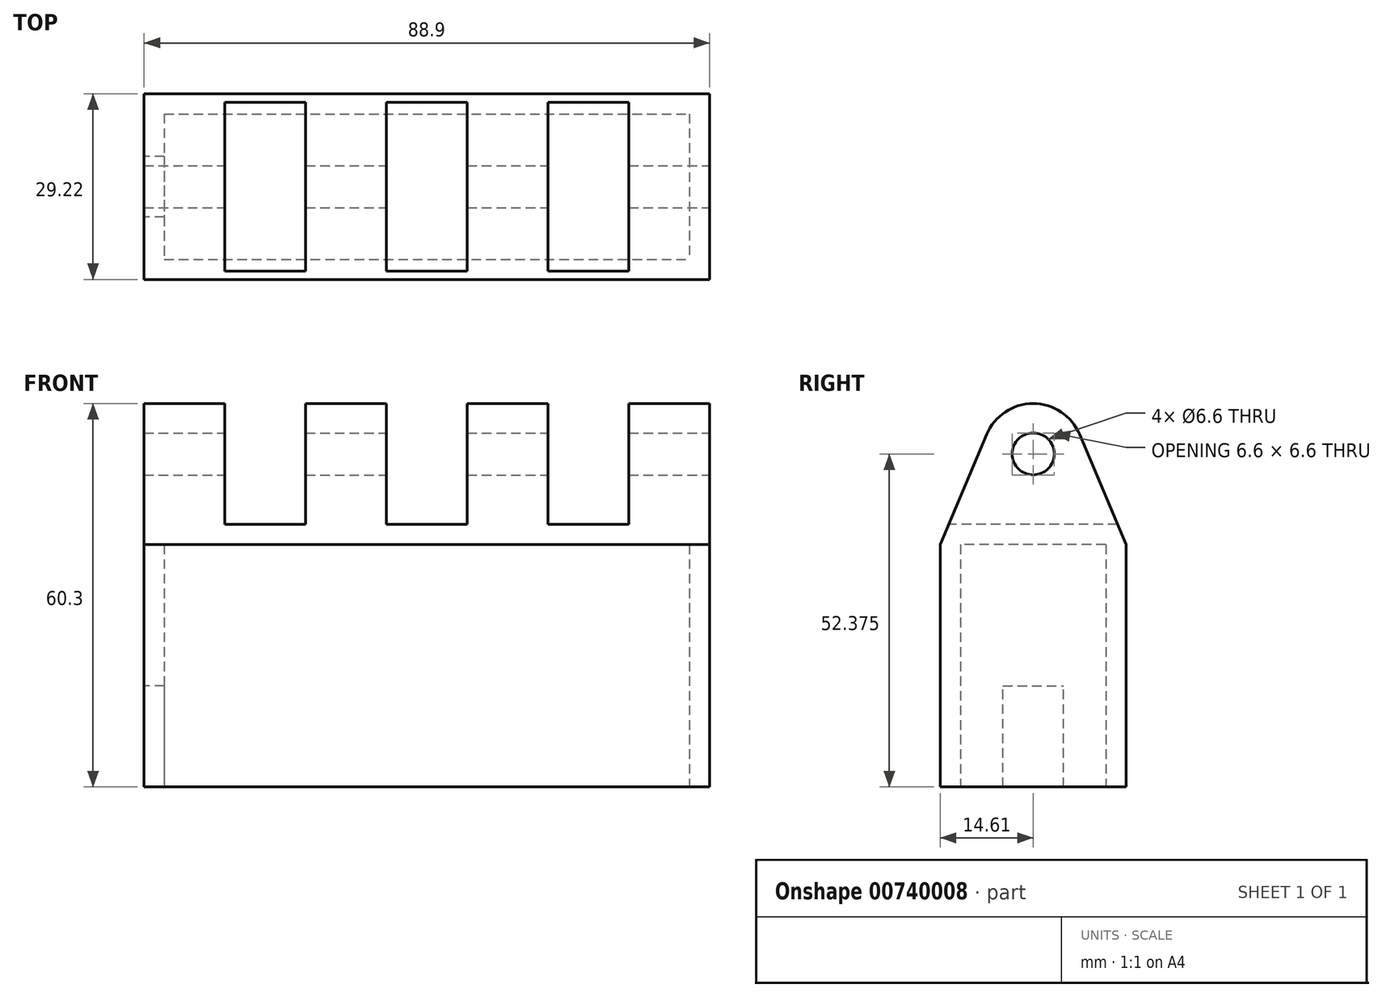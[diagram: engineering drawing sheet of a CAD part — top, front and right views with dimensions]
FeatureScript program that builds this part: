
annotation { "Feature Type Name" : "Feature", "Feature Type Description" : "" }
export const myFeature = defineFeature(function(context is Context, id is Id, definition is map)
    precondition{}
    {
        {
            var Q0;
            Q0=qCreatedBy(makeId("Top.planeOp"),FACE);
            var sketch = newSketch(context, id + "F0", { "sketchPlane" : qUnion([Q0])});
            skLineSegment(sketch, "E0.bottom", {"start": v(-41.28, 11.43) * mm, "end": v(41.28, 11.43) * mm});
            skLineSegment(sketch, "E0.top", {"start": v(-41.28, -11.43) * mm, "end": v(41.28, -11.43) * mm});
            skLineSegment(sketch, "E0.left", {"start": v(-41.28, 11.43) * mm, "end": v(-41.28, -11.43) * mm});
            skLineSegment(sketch, "E0.right", {"start": v(41.28, 11.43) * mm, "end": v(41.28, -11.43) * mm});
            skLineSegment(sketch, "E1.bottom", {"start": v(-44.45, 14.6) * mm, "end": v(44.45, 14.6) * mm});
            skLineSegment(sketch, "E1.top", {"start": v(-44.45, -14.6) * mm, "end": v(44.45, -14.6) * mm});
            skLineSegment(sketch, "E1.left", {"start": v(-44.45, 14.6) * mm, "end": v(-44.45, -14.6) * mm});
            skLineSegment(sketch, "E1.right", {"start": v(44.45, 14.6) * mm, "end": v(44.45, -14.6) * mm});
            skSolve(sketch);
        }
        {
            var Q0;
            Q0=makeQuery(id+"F0.imprint","IMPRINT",FACE,{"disambiguationData":[TD([[makeQuery(id+"F0.imprint","IMPRINT",EDGE,{"derivedFrom":sQuery(id+"F0.wireOp",EDGE,"E0.bottom")}),1.0]])]});
            extrude(context, id + "F1", {"entities" : qUnion([Q0]), "depth" : 38.1 * mm, "offsetDistance" : 25.4 * mm});
        }
        {
            var Q0;
            Q0=makeQuery(id+"F1.opExtrude","SWEPT_FACE",FACE,{"disambiguationData":[OSD([sQuery(id+"F0.wireOp",EDGE,"E1.left")])]});
            var sketch = newSketch(context, id + "F2", { "sketchPlane" : qUnion([Q0])});
            skLineSegment(sketch, "E2.bottom", {"start": v(4.76, 0) * mm, "end": v(-4.76, 0) * mm});
            skLineSegment(sketch, "E2.top", {"start": v(4.76, 15.88) * mm, "end": v(-4.76, 15.88) * mm});
            skLineSegment(sketch, "E2.left", {"start": v(4.76, 0) * mm, "end": v(4.76, 15.88) * mm});
            skLineSegment(sketch, "E2.right", {"start": v(-4.76, 0) * mm, "end": v(-4.76, 15.88) * mm});
            skSolve(sketch);
        }
        {
            var Q0;
            Q0=makeQuery(id+"F2.imprint","IMPRINT",FACE,{"disambiguationData":[TD([[makeQuery(id+"F2.imprint","IMPRINT",EDGE,{"derivedFrom":sQuery(id+"F2.wireOp",EDGE,"E2.bottom")}),1.0]])]});
            extrude(context, id + "F3", {"entities" : qUnion([Q0]), "operationType" : NewBodyOperationType.REMOVE, "oppositeDirection" : true, "depth" : 25.4 * mm, "offsetDistance" : 25.4 * mm});
        }
        {
            var Q0;
            Q0=makeQuery(id+"F1.opExtrude","SWEPT_FACE",FACE,{"disambiguationData":[OSD([sQuery(id+"F0.wireOp",EDGE,"E1.right")])]});
            var sketch = newSketch(context, id + "F4", { "sketchPlane" : qUnion([Q0])});
            skArc(sketch, "E3", {"start": v(7.3, 55.45) * mm, "mid": v(0, 60.3) * mm, "end": v(-7.3, 55.45) * mm});
            skLineSegment(sketch, "E4", {"start": v(-14.6, 38.1) * mm, "end": v(-7.3, 55.45) * mm});
            skLineSegment(sketch, "E5", {"start": v(14.6, 38.1) * mm, "end": v(7.3, 55.45) * mm});
            skLineSegment(sketch, "E6", {"start": v(-14.6, 38.1) * mm, "end": v(14.6, 38.1) * mm});
            skSolve(sketch);
        }
        {
            var Q0;
            Q0=makeQuery(id+"F4.imprint","IMPRINT",FACE,{"disambiguationData":[TD([[makeQuery(id+"F4.imprint","IMPRINT",EDGE,{"derivedFrom":sQuery(id+"F4.wireOp",EDGE,"E3")}),1.0]])]});
            var Q1;
            Q1=makeQuery(id+"F1.opExtrude","SWEPT_FACE",FACE,{"disambiguationData":[OSD([sQuery(id+"F0.wireOp",EDGE,"E1.left")])]});
            extrude(context, id + "F5", {"entities" : qUnion([Q0]), "operationType" : NewBodyOperationType.ADD, "endBound" : BoundingType.UP_TO_SURFACE, "oppositeDirection" : true, "depth" : 25.4 * mm, "endBoundEntityFace" : qUnion([Q1]), "offsetDistance" : 25.4 * mm});
        }
        {
            var Q0;
            Q0=makeQuery(id+"F5.boolean.opBoolean","MERGE",FACE,{"derivedFrom":[makeQuery(id+"F1.opExtrude","SWEPT_FACE",FACE,{"disambiguationData":[OSD([sQuery(id+"F0.wireOp",EDGE,"E1.right")])]}),makeQuery(id+"F5.opExtrude","CAP_FACE",FACE,{"disambiguationData":[OSD([sQuery(id+"F4.wireOp",EDGE,"E3"),sQuery(id+"F4.wireOp",EDGE,"E4"),sQuery(id+"F4.wireOp",EDGE,"E5"),sQuery(id+"F4.wireOp",EDGE,"E6")])],"isStart":true})]});
            var sketch = newSketch(context, id + "F6", { "sketchPlane" : qUnion([Q0])});
            skCircle(sketch, "E7", {"center": v(0, 52.37) * mm, "radius": 3.3 * mm});
            skSolve(sketch);
        }
        {
            var Q0;
            Q0=makeQuery(id+"F6.imprint","IMPRINT",FACE,{"disambiguationData":[TD([[makeQuery(id+"F6.imprint","IMPRINT",EDGE,{"derivedFrom":sQuery(id+"F6.wireOp",EDGE,"E7")}),1.0]])]});
            extrude(context, id + "F7", {"entities" : qUnion([Q0]), "operationType" : NewBodyOperationType.REMOVE, "endBound" : BoundingType.THROUGH_ALL, "oppositeDirection" : true, "depth" : 25.4 * mm, "offsetDistance" : 25.4 * mm});
        }
        {
            var Q0;
            Q0=makeQuery(id+"F1.opExtrude","SWEPT_FACE",FACE,{"disambiguationData":[OSD([sQuery(id+"F0.wireOp",EDGE,"E1.top")])]});
            var sketch = newSketch(context, id + "F8", { "sketchPlane" : qUnion([Q0])});
            skLineSegment(sketch, "E8.bottom", {"start": v(-6.35, 63.5) * mm, "end": v(6.35, 63.5) * mm});
            skLineSegment(sketch, "E8.top", {"start": v(-6.35, 41.27) * mm, "end": v(6.35, 41.27) * mm});
            skLineSegment(sketch, "E8.left", {"start": v(-6.35, 63.5) * mm, "end": v(-6.35, 41.27) * mm});
            skLineSegment(sketch, "E8.right", {"start": v(6.35, 63.5) * mm, "end": v(6.35, 41.27) * mm});
            skLineSegment(sketch, "E9.bottom", {"start": v(19.05, 63.5) * mm, "end": v(31.75, 63.5) * mm});
            skLineSegment(sketch, "E9.top", {"start": v(19.05, 41.27) * mm, "end": v(31.75, 41.27) * mm});
            skLineSegment(sketch, "E9.left", {"start": v(19.05, 63.5) * mm, "end": v(19.05, 41.27) * mm});
            skLineSegment(sketch, "E9.right", {"start": v(31.75, 63.5) * mm, "end": v(31.75, 41.27) * mm});
            skLineSegment(sketch, "E10.bottom", {"start": v(-31.75, 63.5) * mm, "end": v(-19.05, 63.5) * mm});
            skLineSegment(sketch, "E10.top", {"start": v(-31.75, 41.27) * mm, "end": v(-19.05, 41.27) * mm});
            skLineSegment(sketch, "E10.left", {"start": v(-31.75, 63.5) * mm, "end": v(-31.75, 41.27) * mm});
            skLineSegment(sketch, "E10.right", {"start": v(-19.05, 63.5) * mm, "end": v(-19.05, 41.27) * mm});
            skSolve(sketch);
        }
        {
            var Q0;
            Q0=makeQuery(id+"F8.imprint","IMPRINT",FACE,{"disambiguationData":[TD([[makeQuery(id+"F8.imprint","IMPRINT",EDGE,{"derivedFrom":sQuery(id+"F8.wireOp",EDGE,"E10.bottom")}),-1.0]])]});
            var Q1;
            Q1=makeQuery(id+"F8.imprint","IMPRINT",FACE,{"disambiguationData":[TD([[makeQuery(id+"F8.imprint","IMPRINT",EDGE,{"derivedFrom":sQuery(id+"F8.wireOp",EDGE,"E8.bottom")}),-1.0]])]});
            var Q2;
            Q2=makeQuery(id+"F8.imprint","IMPRINT",FACE,{"disambiguationData":[TD([[makeQuery(id+"F8.imprint","IMPRINT",EDGE,{"derivedFrom":sQuery(id+"F8.wireOp",EDGE,"E9.bottom")}),-1.0]])]});
            extrude(context, id + "F9", {"entities" : qUnion([Q0, Q1, Q2]), "operationType" : NewBodyOperationType.REMOVE, "endBound" : BoundingType.THROUGH_ALL, "oppositeDirection" : true, "depth" : 25.4 * mm, "offsetDistance" : 25.4 * mm});
        }
    });
